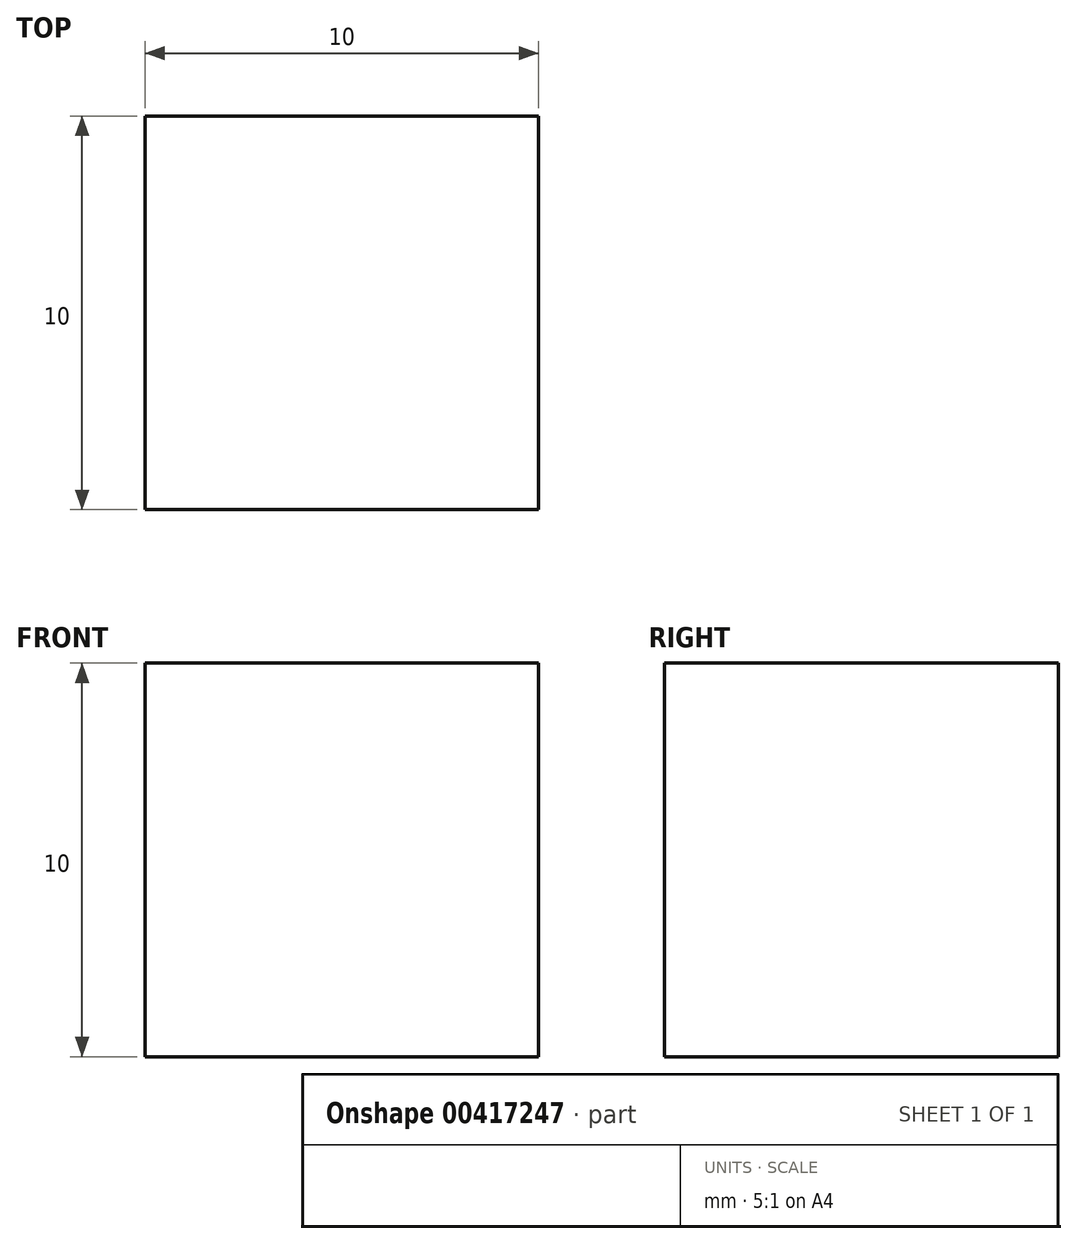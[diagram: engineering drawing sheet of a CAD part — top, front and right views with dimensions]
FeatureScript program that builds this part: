
annotation { "Feature Type Name" : "Feature", "Feature Type Description" : "" }
export const myFeature = defineFeature(function(context is Context, id is Id, definition is map)
    precondition{}
    {
        {
            var Q0;
            Q0=qCreatedBy(makeId("Top.planeOp"),FACE);
            var sketch = newSketch(context, id + "F0", { "sketchPlane" : qUnion([Q0])});
            skLineSegment(sketch, "E0.bottom", {"start": v(-5, -5) * mm, "end": v(5, -5) * mm});
            skLineSegment(sketch, "E0.top", {"start": v(-5, 5) * mm, "end": v(5, 5) * mm});
            skLineSegment(sketch, "E0.left", {"start": v(-5, -5) * mm, "end": v(-5, 5) * mm});
            skLineSegment(sketch, "E0.right", {"start": v(5, -5) * mm, "end": v(5, 5) * mm});
            skPoint(sketch, "E0.middle", {"position": v(0, 0) * mm});
            skSolve(sketch);
        }
        {
            var Q0;
            Q0=makeQuery(id+"F0.imprint","IMPRINT",FACE,{"disambiguationData":[TD([[makeQuery(id+"F0.imprint","IMPRINT",EDGE,{"derivedFrom":sQuery(id+"F0.wireOp",EDGE,"E0.bottom")}),1.0]])]});
            extrude(context, id + "F1", {"entities" : qUnion([Q0]), "endBound" : BoundingType.SYMMETRIC, "depth" : 10 * mm});
        }
    });
